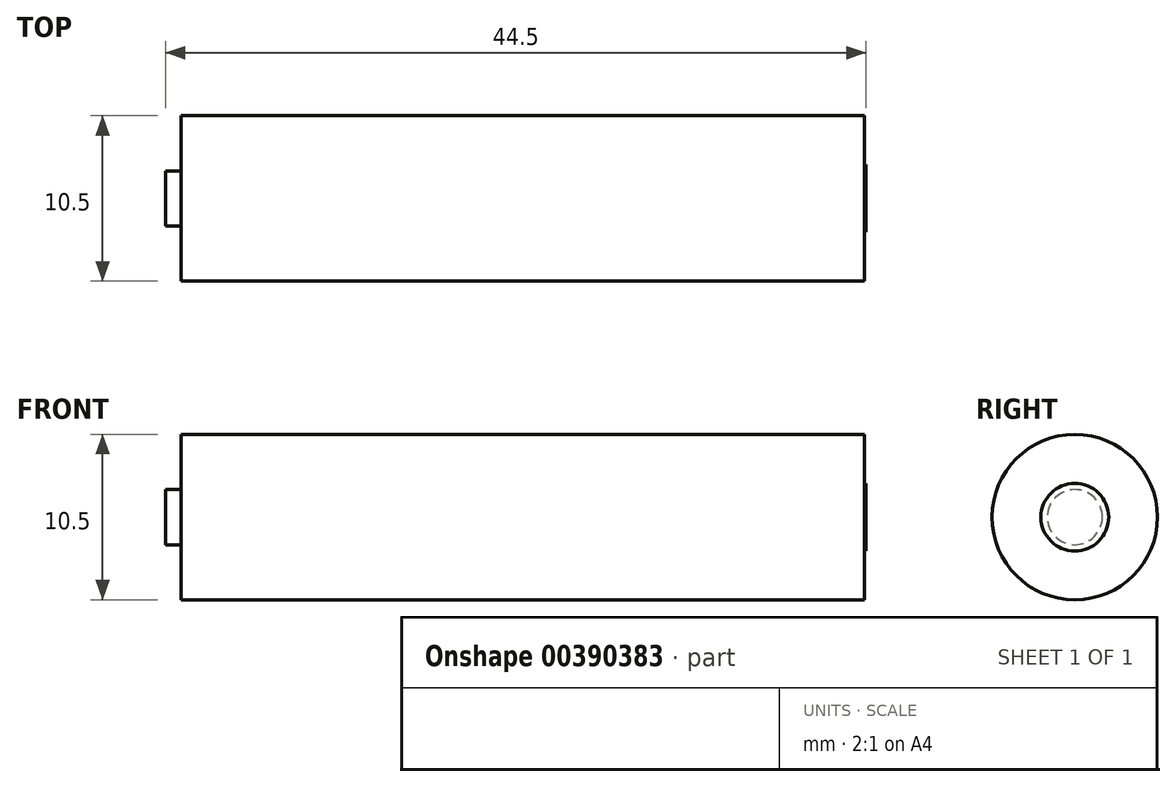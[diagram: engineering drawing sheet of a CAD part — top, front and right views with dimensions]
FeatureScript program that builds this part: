
annotation { "Feature Type Name" : "Feature", "Feature Type Description" : "" }
export const myFeature = defineFeature(function(context is Context, id is Id, definition is map)
    precondition{}
    {
        {
            var Q0;
            Q0=qCreatedBy(makeId("Right.planeOp"),FACE);
            var sketch = newSketch(context, id + "F0", { "sketchPlane" : qUnion([Q0])});
            skCircle(sketch, "E0", {"center": v(0, 0) * mm, "radius": 5.25 * mm});
            skSolve(sketch);
        }
        {
            var Q0;
            Q0=qSketchRegion(id+"F0",true);
            extrude(context, id + "F1", {"entities" : qUnion([Q0]), "endBound" : BoundingType.SYMMETRIC, "depth" : 44.5 * mm});
        }
        {
            var Q0;
            Q0=makeQuery(id+"F1.opExtrude","CAP_FACE",FACE,{"disambiguationData":[OSD([sQuery(id+"F0.wireOp",EDGE,"E0")])],"isStart":false});
            var sketch = newSketch(context, id + "F2", { "sketchPlane" : qUnion([Q0])});
            skCircle(sketch, "E1", {"center": v(0, 0) * mm, "radius": 2.15 * mm});
            skCircle(sketch, "E2.0", {"center": v(0, 0) * mm, "radius": 5.25 * mm});
            skSolve(sketch);
        }
        {
            var Q0;
            Q0=qSketchRegion(id+"F2",true);
            extrude(context, id + "F3", {"entities" : qUnion([Q0]), "operationType" : NewBodyOperationType.REMOVE, "oppositeDirection" : true, "depth" : .1 * mm});
        }
        {
            var Q0;
            Q0=makeQuery(id+"F1.opExtrude","CAP_FACE",FACE,{"disambiguationData":[OSD([sQuery(id+"F0.wireOp",EDGE,"E0")])],"isStart":true});
            var sketch = newSketch(context, id + "F4", { "sketchPlane" : qUnion([Q0])});
            skCircle(sketch, "E3", {"center": v(0, 0) * mm, "radius": 1.75 * mm});
            skCircle(sketch, "E4.0", {"center": v(0, 0) * mm, "radius": 5.25 * mm});
            skSolve(sketch);
        }
        {
            var Q0;
            Q0=qSketchRegion(id+"F4",true);
            extrude(context, id + "F5", {"entities" : qUnion([Q0]), "operationType" : NewBodyOperationType.REMOVE, "oppositeDirection" : true, "depth" : 1 * mm});
        }
    });
